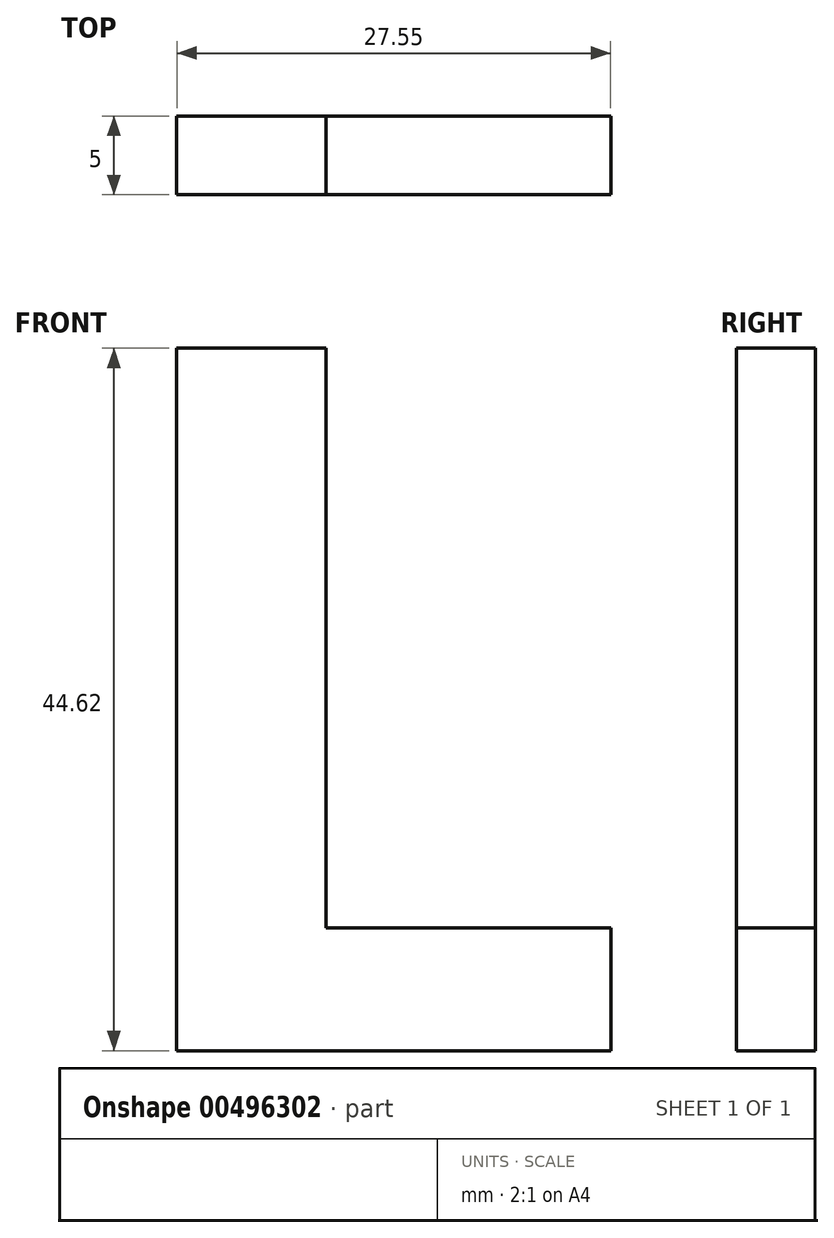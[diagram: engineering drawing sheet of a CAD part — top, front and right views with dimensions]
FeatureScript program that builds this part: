
annotation { "Feature Type Name" : "Feature", "Feature Type Description" : "" }
export const myFeature = defineFeature(function(context is Context, id is Id, definition is map)
    precondition{}
    {
        {
            var Q0;
            Q0=qCreatedBy(makeId("Front.planeOp"),FACE);
            var sketch = newSketch(context, id + "F0", { "sketchPlane" : qUnion([Q0])});
            skText(sketch, "E0", { "text": "L", "fontName": "OpenSans-Bold.ttf"});
            const initialGuessF0  = {"E0": [-0.06175, 0.01278, 1, 0, 0.045]};
            skSetInitialGuess(sketch, initialGuessF0);
            skSolve(sketch);
        }
        {
            var Q0;
            Q0=makeQuery(id+"F0.imprint","IMPRINT",FACE,{"disambiguationData":[TD([[makeQuery(id+"F0.imprint","IMPRINT",EDGE,{"derivedFrom":sQuery(id+"F0.wireOp",EDGE,"E0.sketch_text.stroke-0")}),-1.0]])]});
            extrude(context, id + "F1", {"entities" : qUnion([Q0]), "depth" : 5 * mm});
        }
    });
